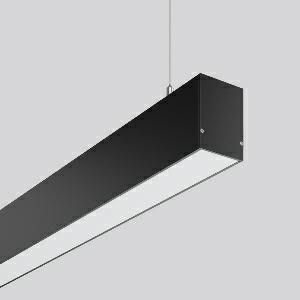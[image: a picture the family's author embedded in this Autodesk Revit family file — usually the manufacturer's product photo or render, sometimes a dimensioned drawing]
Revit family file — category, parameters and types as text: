
# Revit family: less_is_more_50_312315_003_0d84
name_source: partatom
category: Lighting Fixtures
units: mm (PartAtom-declared; Revit-internal decimal feet)

## family parameters
Cut with Voids When Loaded = No
Host = Face
Light Source = No
Part Type = Normal
Room Calculation Point = No
Round Connector Dimension = Use Diameter
Shared = No

## types (1)
- LESS IS MORE 50 (1 x LED Modul 830, 5400 lm, 3000)
    Apparent Load = 47 VA
    CIE Flux Codes = 48 79 95 100 100
    Color Rendering = 80
    Color Temperature = 3000
    Default Elevation = 1800 mm
    Description = Series: LESS IS MORE 50
Linear pendant luminaire for aesthetically sophisticated lighting. Housing: extruded aluminium profile, powder-coated. End cap aluminium powder-coated. Canopy made of aluminium, powder-coated. Diffuser made of non-yellowing plastic (PMMA), opal. Direct light emission. Suitable for pendant. 2-point steel cable suspension freely positionable and infinitely height-adjustable. Special lengths available on request. LED unit with integrated converter interchangeable and removable. Suitable for through-wiring. With sensors or as a safety luminaire on request. 
Colour: deep black, matt (RAL 9005)
Length: 1967 mm
Width: 57 mm
Height: 75 mm
Suspension length: 2000 mm
Lamp: LED
Socket: without socket
Colour temperature: 3000K
Colour rendering index (CRI): 80
System power: 47 W
Rated luminous flux: 5400 lm
Luminous efficiency: 115 lm/W
Control gear: Regulated power supply
Protection class: I
Type of protection: IP 20
    Height = 75 mm
    Lamp = 1 x LED Modul 830
    Lamp Light Flux = 5400 lm
    Lamp count = 1
    Length = 1967 mm
    Lifetime = 50000 h
    Luminous efficacy = 115 lm/W
    Manufacturer = RZB
    ModVariant = No
    Model = 312315.003
    Mounting Place = Ceiling
    Mounting Type = Pendant
    Number of Poles = 1
    OnlyDefault = Yes
    Power Factor = 1
    Product Name = LESS IS MORE 50
    Product group = Pendant LED linear luminaires
    ProductGroupID = 907
    Protection Class = Protection class I
    Protection Degree = IP 20
    RLX_Detail_Level = 1
    RLX_Emergency_Light_Flux = 0 lm
    RLX_Emergency_Type = 0
    RLX_Emergency_Type_DB = No
    RlxData = <blob elided: 28877 chars, md5=cc8a76df>
    Socket = socket
    Standby Power = 0 W
    System Light Flux = 5400 lm
    System Power = 47 W
    Type Comments = Product without accessories
    Type Image = 312318.003.jpg
    URL = http://relux.com
    VarID = ---
    Voltage = 230 V
    Voltage Range = 220-240 V
    Weight = 0.00 kg
    Width = 57 mm

## geometry (parser evidence)
native form markers: Blend x4, Sweep x10
no freeform markers — native parametric forms only
